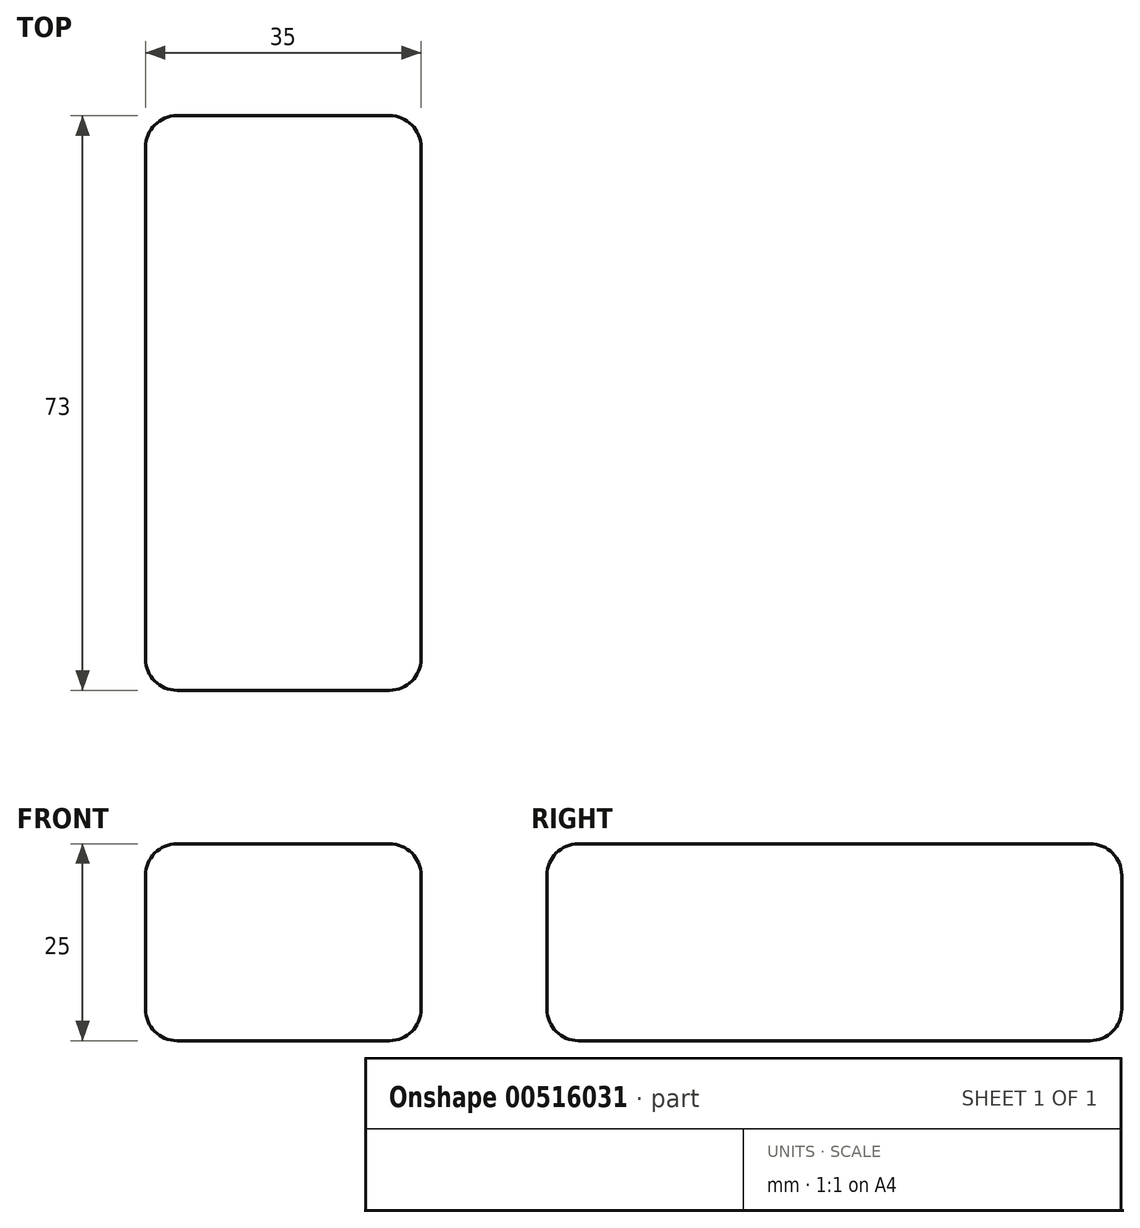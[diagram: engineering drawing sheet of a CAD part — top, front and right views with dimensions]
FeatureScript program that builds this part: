
annotation { "Feature Type Name" : "Feature", "Feature Type Description" : "" }
export const myFeature = defineFeature(function(context is Context, id is Id, definition is map)
    precondition{}
    {
        {
            var Q0;
            Q0=qCreatedBy(makeId("Top.planeOp"),FACE);
            var sketch = newSketch(context, id + "F0", { "sketchPlane" : qUnion([Q0])});
            skLineSegment(sketch, "E0.bottom", {"start": v(-17.5, -36.5) * mm, "end": v(17.5, -36.5) * mm});
            skLineSegment(sketch, "E0.top", {"start": v(-17.5, 36.5) * mm, "end": v(17.5, 36.5) * mm});
            skLineSegment(sketch, "E0.left", {"start": v(-17.5, -36.5) * mm, "end": v(-17.5, 36.5) * mm});
            skLineSegment(sketch, "E0.right", {"start": v(17.5, -36.5) * mm, "end": v(17.5, 36.5) * mm});
            skSolve(sketch);
        }
        {
            var Q0;
            Q0 = qSketchRegion(id + "F0", true);
            extrude(context, id + "F1", {"entities" : qUnion([Q0]), "depth" : 25 * mm, "offsetDistance" : 25 * mm});
        }
        {
            var Q0;
            Q0=makeQuery(id+"F1.opExtrude","CAP_EDGE",EDGE,{"disambiguationData":[OSD([sQuery(id+"F0.wireOp",EDGE,"E0.bottom")])],"isStart":false});
            var Q1;
            Q1=makeQuery(id+"F1.opExtrude","CAP_EDGE",EDGE,{"disambiguationData":[OSD([sQuery(id+"F0.wireOp",EDGE,"E0.right")])],"isStart":false});
            var Q2;
            Q2=makeQuery(id+"F1.opExtrude","CAP_EDGE",EDGE,{"disambiguationData":[OSD([sQuery(id+"F0.wireOp",EDGE,"E0.top")])],"isStart":false});
            var Q3;
            Q3=makeQuery(id+"F1.opExtrude","CAP_EDGE",EDGE,{"disambiguationData":[OSD([sQuery(id+"F0.wireOp",EDGE,"E0.left")])],"isStart":false});
            var Q4;
            Q4=makeQuery(id+"F1.opExtrude","SWEPT_EDGE",EDGE,{"disambiguationData":[OSD([sQuery(id+"F0.wireOp",EDGE,"E0.bottom"),sQuery(id+"F0.wireOp",EDGE,"E0.right")])]});
            var Q5;
            Q5=makeQuery(id+"F1.opExtrude","SWEPT_EDGE",EDGE,{"disambiguationData":[OSD([sQuery(id+"F0.wireOp",EDGE,"E0.bottom"),sQuery(id+"F0.wireOp",EDGE,"E0.left")])]});
            var Q6;
            Q6=makeQuery(id+"F1.opExtrude","SWEPT_EDGE",EDGE,{"disambiguationData":[OSD([sQuery(id+"F0.wireOp",EDGE,"E0.top"),sQuery(id+"F0.wireOp",EDGE,"E0.right")])]});
            var Q7;
            Q7=makeQuery(id+"F1.opExtrude","CAP_EDGE",EDGE,{"disambiguationData":[OSD([sQuery(id+"F0.wireOp",EDGE,"E0.right")])],"isStart":true});
            var Q8;
            Q8=makeQuery(id+"F1.opExtrude","CAP_EDGE",EDGE,{"disambiguationData":[OSD([sQuery(id+"F0.wireOp",EDGE,"E0.bottom")])],"isStart":true});
            var Q9;
            Q9=makeQuery(id+"F1.opExtrude","SWEPT_EDGE",EDGE,{"disambiguationData":[OSD([sQuery(id+"F0.wireOp",EDGE,"E0.top"),sQuery(id+"F0.wireOp",EDGE,"E0.left")])]});
            var Q10;
            Q10=makeQuery(id+"F1.opExtrude","CAP_EDGE",EDGE,{"disambiguationData":[OSD([sQuery(id+"F0.wireOp",EDGE,"E0.top")])],"isStart":true});
            var Q11;
            Q11=makeQuery(id+"F1.opExtrude","CAP_EDGE",EDGE,{"disambiguationData":[OSD([sQuery(id+"F0.wireOp",EDGE,"E0.left")])],"isStart":true});
            fillet(context, id + "F2", {"entities" : qUnion([Q0, Q1, Q2, Q3, Q4, Q5, Q6, Q7, Q8, Q9, Q10, Q11]), "radius" : 4 * mm, "tangentPropagation" : true, "allowEdgeOverflow" : false});
        }
    });
